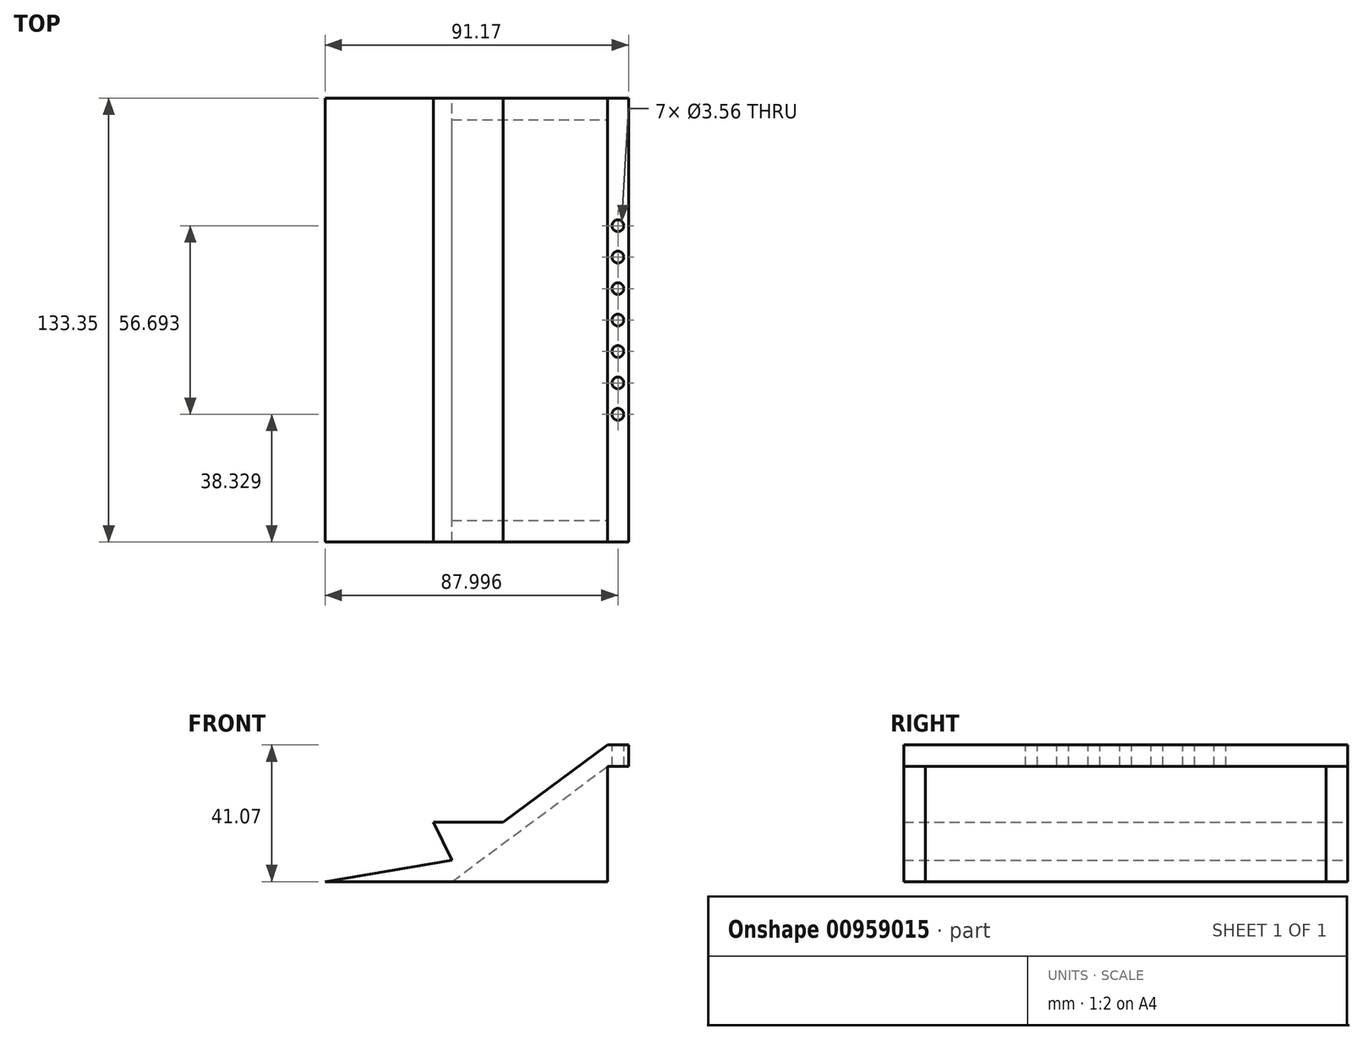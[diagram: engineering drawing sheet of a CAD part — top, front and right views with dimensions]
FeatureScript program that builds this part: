
annotation { "Feature Type Name" : "Feature", "Feature Type Description" : "" }
export const myFeature = defineFeature(function(context is Context, id is Id, definition is map)
    precondition{}
    {
        {
            var Q0;
            Q0=qCreatedBy(makeId("Front.planeOp"),FACE);
            var sketch = newSketch(context, id + "F0", { "sketchPlane" : qUnion([Q0])});
            skLineSegment(sketch, "E0.top", {"start": v(23.36, -17.3) * mm, "end": v(-23.36, -17.3) * mm, "construction": true});
            skLineSegment(sketch, "E0.left", {"start": v(23.36, 17.3) * mm, "end": v(23.36, -17.3) * mm, "construction": true});
            skPoint(sketch, "E0.middle", {"position": v(0, 0) * mm});
            skLineSegment(sketch, "E1", {"start": v(23.36, 17.3) * mm, "end": v(-23.36, -17.3) * mm});
            skLineSegment(sketch, "E2", {"start": v(-23.36, -17.3) * mm, "end": v(-61.46, -17.3) * mm});
            skLineSegment(sketch, "E3", {"start": v(23.36, 23.77) * mm, "end": v(23.36, 17.3) * mm});
            skLineSegment(sketch, "E4", {"start": v(-7.92, 0.6) * mm, "end": v(23.36, 23.77) * mm});
            skLineSegment(sketch, "E5", {"start": v(-61.46, -17.3) * mm, "end": v(-23.36, -10.82) * mm});
            skLineSegment(sketch, "E6", {"start": v(-23.36, 0.6) * mm, "end": v(-7.92, 0.6) * mm});
            skLineSegment(sketch, "E7", {"start": v(-23.36, -10.82) * mm, "end": v(-28.9, 0.6) * mm});
            skLineSegment(sketch, "E8", {"start": v(-28.9, 0.6) * mm, "end": v(-23.36, 0.6) * mm});
            skSolve(sketch);
        }
        {
            var Q0;
            Q0=qSketchRegion(id+"F0",true);
            extrude(context, id + "F1", {"entities" : qUnion([Q0]), "depth" : 133.35 * mm, "offsetDistance" : 25.4 * mm});
        }
        {
            var Q0;
            Q0=makeQuery(id+"F1.opExtrude","SWEPT_FACE",FACE,{"disambiguationData":[OSD([sQuery(id+"F0.wireOp",EDGE,"E3")])]});
            var sketch = newSketch(context, id + "F2", { "sketchPlane" : qUnion([Q0])});
            skLineSegment(sketch, "E9.bottom", {"start": v(-133.35, 23.77) * mm, "end": v(-126.87, 23.77) * mm});
            skLineSegment(sketch, "E9.top", {"start": v(-133.35, -17.3) * mm, "end": v(-126.87, -17.3) * mm});
            skLineSegment(sketch, "E9.left", {"start": v(-133.35, 23.77) * mm, "end": v(-133.35, -17.3) * mm});
            skLineSegment(sketch, "E9.right", {"start": v(-126.87, 23.77) * mm, "end": v(-126.87, -17.3) * mm});
            skLineSegment(sketch, "E10", {"start": v(-66.68, 23.77) * mm, "end": v(-66.68, -22.6) * mm});
            skLineSegment(sketch, "E11.MirrorCS", {"start": v(0, -17.3) * mm, "end": v(-6.48, -17.3) * mm});
            skLineSegment(sketch, "E12.MirrorCS", {"start": v(-6.48, 23.77) * mm, "end": v(-6.48, -17.3) * mm});
            skLineSegment(sketch, "E13.MirrorCS", {"start": v(0, 23.77) * mm, "end": v(0, -17.3) * mm});
            skLineSegment(sketch, "E14.MirrorCS", {"start": v(0, 23.77) * mm, "end": v(-6.48, 23.77) * mm});
            skSolve(sketch);
        }
        {
            var Q0;
            {var subQ0=sQuery(id+"F2.wireOp",EDGE,"E9.top");Q0=makeQuery(id+"F2.imprint","IMPRINT",FACE,{"disambiguationData":[TD([[makeQuery(id+"F2.imprint","IMPRINT",EDGE,{"derivedFrom":subQ0}),1.0]])]});}
            var Q1;
            {var subQ0=sQuery(id+"F2.wireOp",EDGE,"E11.MirrorCS");Q1=makeQuery(id+"F2.imprint","IMPRINT",FACE,{"disambiguationData":[TD([[makeQuery(id+"F2.imprint","IMPRINT",EDGE,{"derivedFrom":subQ0}),-1.0]])]});}
            var Q2;
            Q2=makeQuery(id+"F1.opExtrude","SWEPT_BODY",BODY,{"disambiguationData":[OSD([sQuery(id+"F0.wireOp",EDGE,"E1"),sQuery(id+"F0.wireOp",EDGE,"E2"),sQuery(id+"F0.wireOp",EDGE,"E3"),sQuery(id+"F0.wireOp",EDGE,"E4"),sQuery(id+"F0.wireOp",EDGE,"E5")])]});
            extrude(context, id + "F3", {"entities" : qUnion([Q0, Q1]), "operationType" : NewBodyOperationType.ADD, "endBound" : BoundingType.UP_TO_BODY, "oppositeDirection" : true, "depth" : 25.4 * mm, "endBoundEntityBody" : qUnion([Q2]), "offsetDistance" : 25.4 * mm});
        }
        {
            var Q0;
            {var subQ0=sQuery(id+"F0.wireOp",EDGE,"E3");var subQ1=sQuery(id+"F0.wireOp",EDGE,"E1");Q0=makeQuery(id+"F3.boolean.opBoolean","MERGE",FACE,{"derivedFrom":[makeQuery(id+"F1.opExtrude","SWEPT_FACE",FACE,{"disambiguationData":[OSD([subQ0])]}),makeQuery(id+"F3.opExtrude","CAP_FACE",FACE,{"disambiguationData":[OSD([subQ1,subQ0,sQuery(id+"F2.wireOp",EDGE,"E9.top"),sQuery(id+"F2.wireOp",EDGE,"E9.left"),sQuery(id+"F2.wireOp",EDGE,"E9.right")])],"isStart":true}),makeQuery(id+"F3.opExtrude","CAP_FACE",FACE,{"disambiguationData":[OSD([subQ1,subQ0,sQuery(id+"F2.wireOp",EDGE,"E11.MirrorCS"),sQuery(id+"F2.wireOp",EDGE,"E12.MirrorCS"),sQuery(id+"F2.wireOp",EDGE,"E13.MirrorCS")])],"isStart":true})]});}
            var sketch = newSketch(context, id + "F4", { "sketchPlane" : qUnion([Q0])});
            skLineSegment(sketch, "E15.bottom", {"start": v(-133.35, 23.77) * mm, "end": v(0, 23.77) * mm});
            skLineSegment(sketch, "E15.top", {"start": v(-133.35, 17.3) * mm, "end": v(0, 17.3) * mm});
            skLineSegment(sketch, "E15.left", {"start": v(-133.35, 23.77) * mm, "end": v(-133.35, 17.3) * mm});
            skLineSegment(sketch, "E15.right", {"start": v(0, 23.77) * mm, "end": v(0, 17.3) * mm});
            skSolve(sketch);
        }
        {
            var Q0;
            Q0=makeQuery(id+"F4.imprint","IMPRINT",FACE,{"disambiguationData":[TD([[makeQuery(id+"F4.imprint","IMPRINT",EDGE,{"derivedFrom":sQuery(id+"F4.wireOp",EDGE,"E15.bottom")}),-1.0]])]});
            extrude(context, id + "F5", {"entities" : qUnion([Q0]), "operationType" : NewBodyOperationType.ADD, "depth" : 6.35 * mm, "offsetDistance" : 25.4 * mm});
        }
        {
            var Q0;
            Q0=makeQuery(id+"F5.opExtrude","SWEPT_FACE",FACE,{"disambiguationData":[OSD([sQuery(id+"F4.wireOp",EDGE,"E15.bottom")])]});
            var sketch = newSketch(context, id + "F6", { "sketchPlane" : qUnion([Q0])});
            skLineSegment(sketch, "E16", {"start": v(26.54, 0) * mm, "end": v(26.54, -133.35) * mm, "construction": true});
            skCircle(sketch, "E17", {"center": v(26.54, -66.68) * mm, "radius": 1.78 * mm});
            skCircle(sketch, "E18", {"center": v(26.54, -57.23) * mm, "radius": 1.78 * mm});
            skCircle(sketch, "E19", {"center": v(26.54, -47.78) * mm, "radius": 1.78 * mm});
            skCircle(sketch, "E20", {"center": v(26.54, -76.12) * mm, "radius": 1.78 * mm});
            skCircle(sketch, "E21", {"center": v(26.54, -85.57) * mm, "radius": 1.78 * mm});
            skCircle(sketch, "E22", {"center": v(26.54, -38.33) * mm, "radius": 1.78 * mm});
            skCircle(sketch, "E23", {"center": v(26.54, -95.02) * mm, "radius": 1.78 * mm});
            skSolve(sketch);
        }
        {
            var Q0;
            Q0=makeQuery(id+"F6.imprint","IMPRINT",FACE,{"disambiguationData":[TD([[makeQuery(id+"F6.imprint","IMPRINT",EDGE,{"derivedFrom":sQuery(id+"F6.wireOp",EDGE,"E22")}),1.0]])]});
            var Q1;
            Q1=makeQuery(id+"F6.imprint","IMPRINT",FACE,{"disambiguationData":[TD([[makeQuery(id+"F6.imprint","IMPRINT",EDGE,{"derivedFrom":sQuery(id+"F6.wireOp",EDGE,"E19")}),1.0]])]});
            var Q2;
            Q2=makeQuery(id+"F6.imprint","IMPRINT",FACE,{"disambiguationData":[TD([[makeQuery(id+"F6.imprint","IMPRINT",EDGE,{"derivedFrom":sQuery(id+"F6.wireOp",EDGE,"E18")}),1.0]])]});
            var Q3;
            Q3=makeQuery(id+"F6.imprint","IMPRINT",FACE,{"disambiguationData":[TD([[makeQuery(id+"F6.imprint","IMPRINT",EDGE,{"derivedFrom":sQuery(id+"F6.wireOp",EDGE,"E17")}),1.0]])]});
            var Q4;
            Q4=makeQuery(id+"F6.imprint","IMPRINT",FACE,{"disambiguationData":[TD([[makeQuery(id+"F6.imprint","IMPRINT",EDGE,{"derivedFrom":sQuery(id+"F6.wireOp",EDGE,"E20")}),1.0]])]});
            var Q5;
            Q5=makeQuery(id+"F6.imprint","IMPRINT",FACE,{"disambiguationData":[TD([[makeQuery(id+"F6.imprint","IMPRINT",EDGE,{"derivedFrom":sQuery(id+"F6.wireOp",EDGE,"E21")}),1.0]])]});
            var Q6;
            Q6=makeQuery(id+"F6.imprint","IMPRINT",FACE,{"disambiguationData":[TD([[makeQuery(id+"F6.imprint","IMPRINT",EDGE,{"derivedFrom":sQuery(id+"F6.wireOp",EDGE,"E23")}),1.0]])]});
            extrude(context, id + "F7", {"entities" : qUnion([Q0, Q1, Q2, Q3, Q4, Q5, Q6]), "operationType" : NewBodyOperationType.REMOVE, "oppositeDirection" : true, "depth" : 25.4 * mm, "offsetDistance" : 25.4 * mm});
        }
    });
